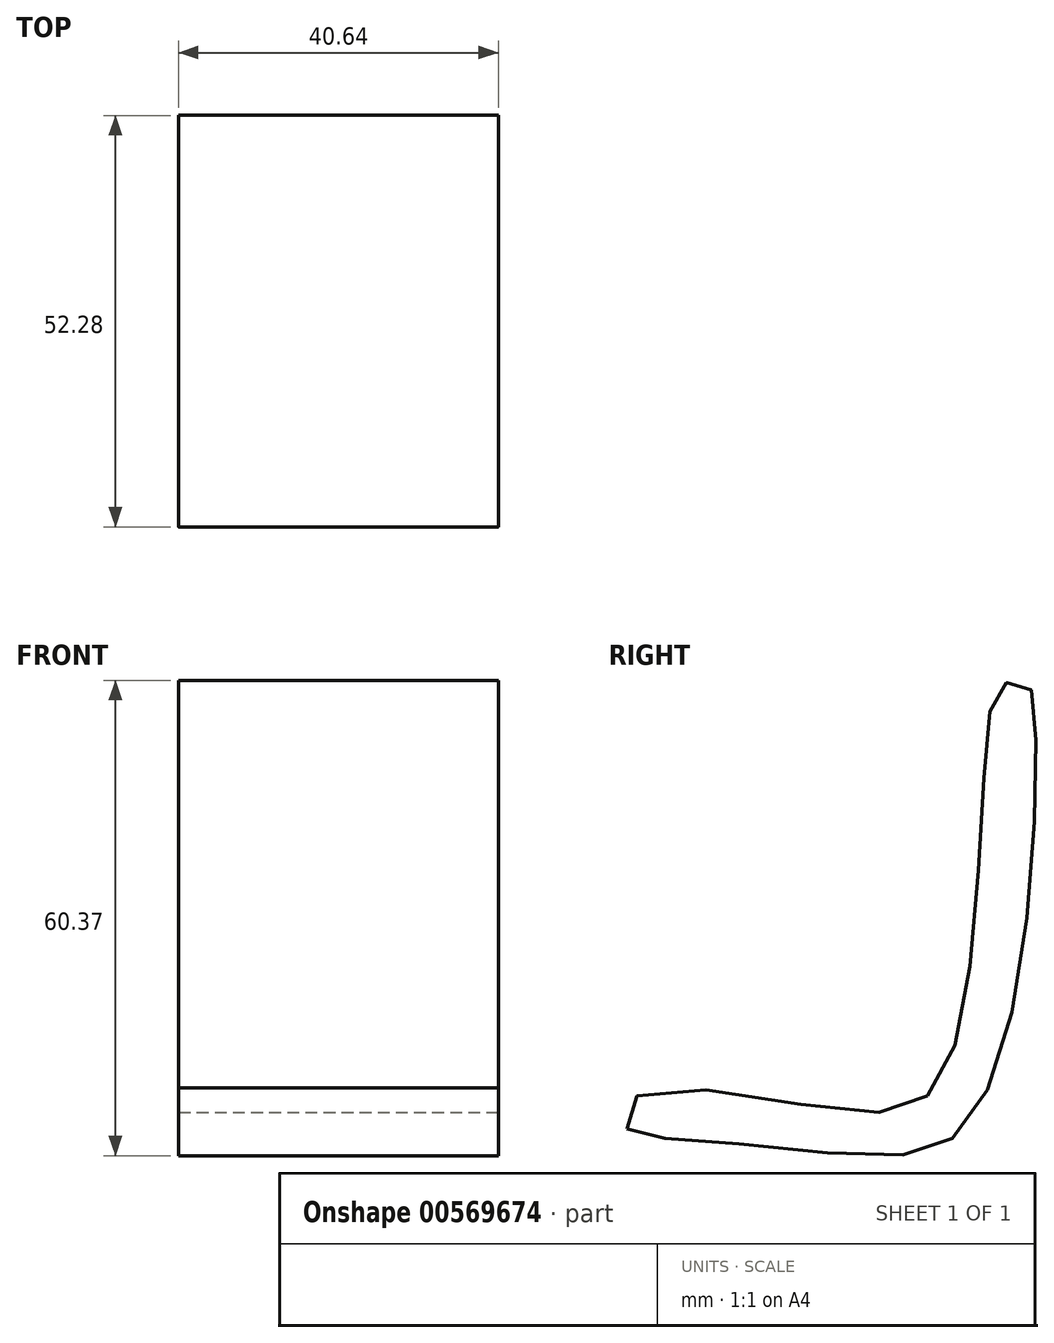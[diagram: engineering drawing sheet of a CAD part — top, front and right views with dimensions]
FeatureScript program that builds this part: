
annotation { "Feature Type Name" : "Feature", "Feature Type Description" : "" }
export const myFeature = defineFeature(function(context is Context, id is Id, definition is map)
    precondition{}
    {
        {
            var Q0;
            Q0=qCreatedBy(makeId("Right.planeOp"),FACE);
            var sketch = newSketch(context, id + "F0", { "sketchPlane" : qUnion([Q0])});
            skFitSpline(sketch, "E0", {"points": [v(-26.89, -6.9) * mm, v(-25.57, -2.68) * mm, v(0, -4.52) * mm, v(11.58, -2.41) * mm, v(16.85, 15.24) * mm, v(18.96, 44.23) * mm, v(20.8, 49.5) * mm, v(23.7, 49.76) * mm, v(25.02, 43.7) * mm, v(23.17, 14.19) * mm, v(15.8, -6.9) * mm, v(5.78, -10.32) * mm, v(-19.77, -8.2) * mm, v(-26.89, -6.9) * mm]});
            skSolve(sketch);
        }
        {
            var Q0;
            Q0=makeQuery(id+"F0.imprint","IMPRINT",FACE,{"disambiguationData":[TD([[makeQuery(id+"F0.imprint","IMPRINT",EDGE,{"derivedFrom":sQuery(id+"F0.wireOp",EDGE,"E0")}),-1.0]])]});
            extrude(context, id + "F1", {"entities" : qUnion([Q0]), "depth" : 40.64 * mm, "offsetDistance" : 25.4 * mm});
        }
    });
